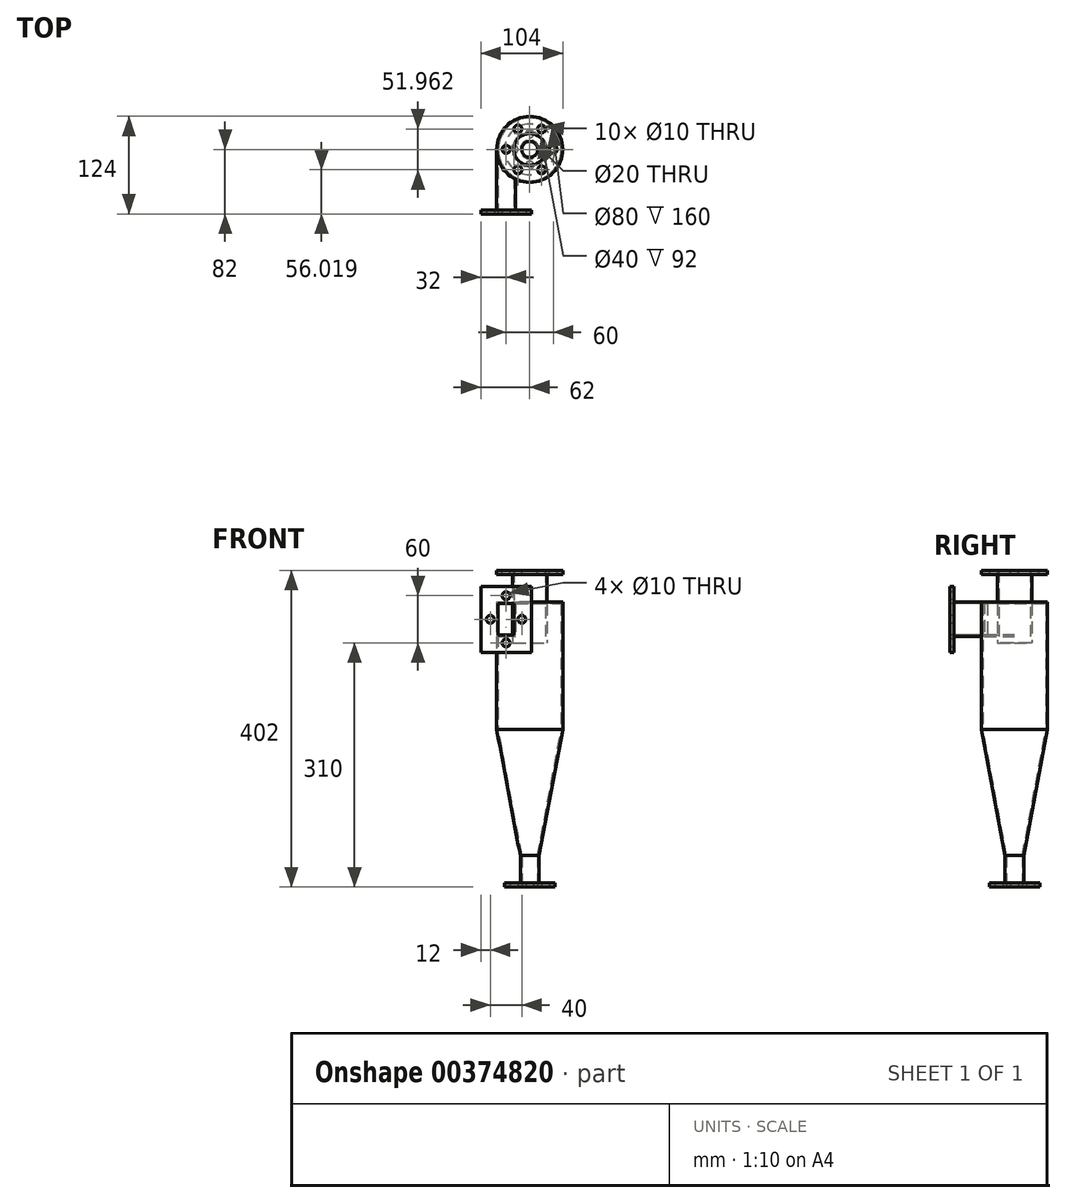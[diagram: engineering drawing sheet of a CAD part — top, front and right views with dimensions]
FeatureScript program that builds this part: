
annotation { "Feature Type Name" : "Feature", "Feature Type Description" : "" }
export const myFeature = defineFeature(function(context is Context, id is Id, definition is map)
    precondition{}
    {
        {
            var Q0;
            Q0=qCreatedBy(makeId("Front.planeOp"),FACE);
            var sketch = newSketch(context, id + "F0", { "sketchPlane" : qUnion([Q0])});
            skLineSegment(sketch, "E0", {"start": v(-40, 360) * mm, "end": v(-40, 200) * mm});
            skLineSegment(sketch, "E1", {"start": v(-40, 200) * mm, "end": v(-10, 40) * mm});
            skLineSegment(sketch, "E2", {"start": v(-10, 40) * mm, "end": v(-10, 0) * mm});
            skLineSegment(sketch, "E3", {"start": v(-40, 360) * mm, "end": v(-22, 360) * mm});
            skLineSegment(sketch, "E4", {"start": v(-10, 0) * mm, "end": v(0, 0) * mm, "construction": true});
            skLineSegment(sketch, "E5", {"start": v(-20, 310) * mm, "end": v(0, 310) * mm, "construction": true});
            skLineSegment(sketch, "E6", {"start": v(0, 0) * mm, "end": v(0, 360) * mm, "construction": true});
            skLineSegment(sketch, "E7.0", {"start": v(-42, 362) * mm, "end": v(-22, 362) * mm});
            skLineSegment(sketch, "E7.1", {"start": v(-42, 362) * mm, "end": v(-42, 199.81) * mm});
            skLineSegment(sketch, "E7.2", {"start": v(-42, 199.81) * mm, "end": v(-12, 39.81) * mm});
            skLineSegment(sketch, "E7.3", {"start": v(-12, 39.81) * mm, "end": v(-12, 0) * mm});
            skLineSegment(sketch, "E8", {"start": v(-22, 362) * mm, "end": v(-22, 402) * mm});
            skLineSegment(sketch, "E9", {"start": v(-22, 402) * mm, "end": v(-20, 402) * mm});
            skLineSegment(sketch, "E10", {"start": v(-20, 402) * mm, "end": v(-20, 360) * mm});
            skLineSegment(sketch, "E11", {"start": v(-20, 310) * mm, "end": v(-20, 310) * mm});
            skLineSegment(sketch, "E12", {"start": v(-12, 0) * mm, "end": v(-10, 0) * mm});
            skLineSegment(sketch, "E13", {"start": v(-22, 360) * mm, "end": v(-22, 310) * mm});
            skLineSegment(sketch, "E14", {"start": v(-20, 310) * mm, "end": v(-22, 310) * mm});
            skPoint(sketch, "E15.end.orphan", {"position": v(-20, 360) * mm});
            skLineSegment(sketch, "E16", {"start": v(-20, 360) * mm, "end": v(-20, 310) * mm});
            skSolve(sketch);
        }
        {
            var Q0;
            Q0=makeQuery(id+"F0.imprint","IMPRINT",FACE,{"disambiguationData":[TD([[makeQuery(id+"F0.imprint","IMPRINT",EDGE,{"derivedFrom":sQuery(id+"F0.wireOp",EDGE,"E0")}),-1.0]])]});
            var Q1;
            Q1=sQuery(id+"F0.wireOp",EDGE,"E6");
            revolve(context, id + "F1", {"entities" : qUnion([Q0]), "axis" : qUnion([Q1]), "revolveType" : RevolveType.FULL});
        }
        {
            var Q0;
            Q0=qCreatedBy(makeId("Front.planeOp"),FACE);
            cPlane(context, id + "F2", {"entities" : qUnion([Q0]), "cplaneType" : CPlaneType.OFFSET, "offset" : 42 * mm, "width" : 152.4 * mm, "height" : 152.4 * mm});
        }
        {
            var Q0;
            Q0=qCreatedBy(id+"F2.planeOp",FACE);
            var sketch = newSketch(context, id + "F3", { "sketchPlane" : qUnion([Q0])});
            skLineSegment(sketch, "E17", {"start": v(0, 0) * mm, "end": v(0, 400.72) * mm, "construction": true});
            skLineSegment(sketch, "E18.bottom", {"start": v(-40, 360) * mm, "end": v(-20, 360) * mm});
            skLineSegment(sketch, "E18.top", {"start": v(-40, 320) * mm, "end": v(-20, 320) * mm});
            skLineSegment(sketch, "E18.left", {"start": v(-40, 360) * mm, "end": v(-40, 320) * mm});
            skLineSegment(sketch, "E18.right", {"start": v(-20, 360) * mm, "end": v(-20, 320) * mm});
            skLineSegment(sketch, "E19.0", {"start": v(-42, 362) * mm, "end": v(-18, 362) * mm});
            skLineSegment(sketch, "E19.1", {"start": v(-42, 362) * mm, "end": v(-42, 318) * mm});
            skLineSegment(sketch, "E19.2", {"start": v(-42, 318) * mm, "end": v(-18, 318) * mm});
            skLineSegment(sketch, "E19.3", {"start": v(-18, 362) * mm, "end": v(-18, 318) * mm});
            skSolve(sketch);
        }
        {
            var Q0;
            Q0=makeQuery(id+"F3.imprint","IMPRINT",FACE,{"disambiguationData":[TD([[makeQuery(id+"F3.imprint","IMPRINT",EDGE,{"derivedFrom":sQuery(id+"F3.wireOp",EDGE,"E18.bottom")}),1.0]])]});
            var Q1;
            Q1=makeQuery(id+"F1.opRevolve","SWEPT_FACE",FACE,{"disambiguationData":[OSD([sQuery(id+"F0.wireOp",EDGE,"E7.1")])]});
            extrude(context, id + "F4", {"entities" : qUnion([Q0]), "operationType" : NewBodyOperationType.ADD, "endBound" : BoundingType.UP_TO_SURFACE, "oppositeDirection" : true, "endBoundEntityFace" : qUnion([Q1]), "depth" : 25.4 * mm});
        }
        {
            var Q0;
            Q0=makeQuery(id+"F4.opExtrude","CAP_FACE",FACE,{"disambiguationData":[OSD([sQuery(id+"F3.wireOp",EDGE,"E18.bottom"),sQuery(id+"F3.wireOp",EDGE,"E18.top"),sQuery(id+"F3.wireOp",EDGE,"E18.left"),sQuery(id+"F3.wireOp",EDGE,"E18.right"),sQuery(id+"F3.wireOp",EDGE,"E19.0"),sQuery(id+"F3.wireOp",EDGE,"E19.1"),sQuery(id+"F3.wireOp",EDGE,"E19.2"),sQuery(id+"F3.wireOp",EDGE,"E19.3")])],"isStart":true});
            var sketch = newSketch(context, id + "F5", { "sketchPlane" : qUnion([Q0])});
            skLineSegment(sketch, "E20", {"start": v(-40, 360) * mm, "end": v(-20, 360) * mm});
            skLineSegment(sketch, "E21", {"start": v(-20, 360) * mm, "end": v(-20, 320) * mm});
            skLineSegment(sketch, "E22", {"start": v(-20, 320) * mm, "end": v(-40, 320) * mm});
            skLineSegment(sketch, "E23", {"start": v(-40, 320) * mm, "end": v(-40, 360) * mm});
            skSolve(sketch);
        }
        {
            var Q0;
            Q0=qSketchRegion(id+"F5",true);
            var Q1;
            Q1=makeQuery(id+"F1.opRevolve","SWEPT_FACE",FACE,{"disambiguationData":[OSD([sQuery(id+"F0.wireOp",EDGE,"E0")])]});
            extrude(context, id + "F6", {"entities" : qUnion([Q0]), "operationType" : NewBodyOperationType.REMOVE, "endBound" : BoundingType.UP_TO_SURFACE, "oppositeDirection" : true, "endBoundEntityFace" : qUnion([Q1]), "depth" : 25.4 * mm});
        }
        {
            var Q0;
            Q0=makeQuery(id+"F4.opExtrude","CAP_FACE",FACE,{"disambiguationData":[OSD([sQuery(id+"F3.wireOp",EDGE,"E18.bottom"),sQuery(id+"F3.wireOp",EDGE,"E18.top"),sQuery(id+"F3.wireOp",EDGE,"E18.left"),sQuery(id+"F3.wireOp",EDGE,"E18.right"),sQuery(id+"F3.wireOp",EDGE,"E19.0"),sQuery(id+"F3.wireOp",EDGE,"E19.1"),sQuery(id+"F3.wireOp",EDGE,"E19.2"),sQuery(id+"F3.wireOp",EDGE,"E19.3")])],"isStart":true});
            extrude(context, id + "F7", {"entities" : qUnion([Q0]), "operationType" : NewBodyOperationType.ADD, "depth" : 40 * mm});
        }
        {
            var Q0;
            Q0=makeQuery(id+"F7.opExtrude","CAP_FACE",FACE,{"disambiguationData":[OSD([sQuery(id+"F3.wireOp",EDGE,"E18.bottom"),sQuery(id+"F3.wireOp",EDGE,"E18.top"),sQuery(id+"F3.wireOp",EDGE,"E18.left"),sQuery(id+"F3.wireOp",EDGE,"E18.right"),sQuery(id+"F3.wireOp",EDGE,"E19.0"),sQuery(id+"F3.wireOp",EDGE,"E19.1"),sQuery(id+"F3.wireOp",EDGE,"E19.2"),sQuery(id+"F3.wireOp",EDGE,"E19.3")])],"isStart":false});
            var sketch = newSketch(context, id + "F8", { "sketchPlane" : qUnion([Q0])});
            skLineSegment(sketch, "E24", {"start": v(-40, 360) * mm, "end": v(-20, 320) * mm, "construction": true});
            skLineSegment(sketch, "E25", {"start": v(-20, 360) * mm, "end": v(-40, 320) * mm, "construction": true});
            skLineSegment(sketch, "E26.bottom", {"start": v(2, 382) * mm, "end": v(-62, 382) * mm});
            skLineSegment(sketch, "E26.top", {"start": v(2, 298) * mm, "end": v(-62, 298) * mm});
            skLineSegment(sketch, "E26.left", {"start": v(2, 382) * mm, "end": v(2, 298) * mm});
            skLineSegment(sketch, "E26.right", {"start": v(-62, 382) * mm, "end": v(-62, 298) * mm});
            skPoint(sketch, "E26.middle", {"position": v(-30, 340) * mm});
            skSolve(sketch);
        }
        {
            var Q0;
            Q0=makeQuery(id+"F8.imprint","IMPRINT",FACE,{"disambiguationData":[TD([[makeQuery(id+"F8.imprint","IMPRINT",EDGE,{"derivedFrom":sQuery(id+"F8.wireOp",EDGE,"E26.bottom")}),1.0]])]});
            extrude(context, id + "F9", {"entities" : qUnion([Q0]), "operationType" : NewBodyOperationType.ADD, "oppositeDirection" : true, "depth" : 5 * mm});
        }
        {
            var Q0;
            Q0=makeQuery(id+"F1.opRevolve","SWEPT_FACE",FACE,{"disambiguationData":[OSD([sQuery(id+"F0.wireOp",EDGE,"E12")])]});
            var sketch = newSketch(context, id + "F10", { "sketchPlane" : qUnion([Q0])});
            skCircle(sketch, "E27", {"center": v(0, 0) * mm, "radius": 32 * mm});
            skSolve(sketch);
        }
        {
            var Q0;
            Q0=makeQuery(id+"F10.imprint","IMPRINT",FACE,{"disambiguationData":[TD([[makeQuery(id+"F10.imprint","IMPRINT",EDGE,{"derivedFrom":sQuery(id+"F10.wireOp",EDGE,"E27")}),1.0]])]});
            extrude(context, id + "F11", {"entities" : qUnion([Q0]), "operationType" : NewBodyOperationType.ADD, "oppositeDirection" : true, "depth" : 5 * mm});
        }
        {
            var Q0;
            {var subQ0=sQuery(id+"F3.wireOp",EDGE,"E19.3");var subQ1=sQuery(id+"F3.wireOp",EDGE,"E19.2");var subQ2=sQuery(id+"F3.wireOp",EDGE,"E19.1");var subQ3=sQuery(id+"F3.wireOp",EDGE,"E19.0");Q0=makeQuery(id+"F9.boolean.opBoolean","MERGE",FACE,{"derivedFrom":[makeQuery(id+"F7.opExtrude","CAP_FACE",FACE,{"disambiguationData":[OSD([sQuery(id+"F3.wireOp",EDGE,"E18.bottom"),sQuery(id+"F3.wireOp",EDGE,"E18.top"),sQuery(id+"F3.wireOp",EDGE,"E18.left"),sQuery(id+"F3.wireOp",EDGE,"E18.right"),subQ3,subQ2,subQ1,subQ0])],"isStart":false}),makeQuery(id+"F9.opExtrude","CAP_FACE",FACE,{"disambiguationData":[OSD([subQ3,subQ2,subQ1,subQ0,sQuery(id+"F8.wireOp",EDGE,"E26.bottom"),sQuery(id+"F8.wireOp",EDGE,"E26.top"),sQuery(id+"F8.wireOp",EDGE,"E26.left"),sQuery(id+"F8.wireOp",EDGE,"E26.right")])],"isStart":true})]});}
            var sketch = newSketch(context, id + "F12", { "sketchPlane" : qUnion([Q0])});
            skLineSegment(sketch, "E28", {"start": v(-40, 360) * mm, "end": v(-20, 320) * mm, "construction": true});
            skLineSegment(sketch, "E29", {"start": v(-20, 360) * mm, "end": v(-40, 320) * mm, "construction": true});
            skLineSegment(sketch, "E30", {"start": v(-30, 340) * mm, "end": v(-30, 370) * mm, "construction": true});
            skPoint(sketch, "E30.endSnap0", {"position": v(-30, 360) * mm});
            skLineSegment(sketch, "E31", {"start": v(-30, 340) * mm, "end": v(-30, 310) * mm, "construction": true});
            skLineSegment(sketch, "E32", {"start": v(-30, 340) * mm, "end": v(-50, 340) * mm, "construction": true});
            skLineSegment(sketch, "E33", {"start": v(-30, 340) * mm, "end": v(-10, 340) * mm, "construction": true});
            skCircle(sketch, "E34", {"center": v(-30, 370) * mm, "radius": 5 * mm});
            skCircle(sketch, "E35", {"center": v(-10, 340) * mm, "radius": 5 * mm});
            skCircle(sketch, "E36", {"center": v(-50, 340) * mm, "radius": 5 * mm});
            skCircle(sketch, "E37", {"center": v(-30, 310) * mm, "radius": 5 * mm});
            skSolve(sketch);
        }
        {
            var Q0;
            Q0=makeQuery(id+"F12.imprint","IMPRINT",FACE,{"disambiguationData":[TD([[makeQuery(id+"F12.imprint","IMPRINT",EDGE,{"derivedFrom":sQuery(id+"F12.wireOp",EDGE,"E34")}),1.0]])]});
            var Q1;
            Q1=makeQuery(id+"F12.imprint","IMPRINT",FACE,{"disambiguationData":[TD([[makeQuery(id+"F12.imprint","IMPRINT",EDGE,{"derivedFrom":sQuery(id+"F12.wireOp",EDGE,"E35")}),1.0]])]});
            var Q2;
            Q2=makeQuery(id+"F12.imprint","IMPRINT",FACE,{"disambiguationData":[TD([[makeQuery(id+"F12.imprint","IMPRINT",EDGE,{"derivedFrom":sQuery(id+"F12.wireOp",EDGE,"E37")}),1.0]])]});
            var Q3;
            Q3=makeQuery(id+"F12.imprint","IMPRINT",FACE,{"disambiguationData":[TD([[makeQuery(id+"F12.imprint","IMPRINT",EDGE,{"derivedFrom":sQuery(id+"F12.wireOp",EDGE,"E36")}),1.0]])]});
            var Q4;
            Q4=makeQuery(id+"F9.opExtrude","CAP_FACE",FACE,{"disambiguationData":[OSD([sQuery(id+"F3.wireOp",EDGE,"E19.0"),sQuery(id+"F3.wireOp",EDGE,"E19.1"),sQuery(id+"F3.wireOp",EDGE,"E19.2"),sQuery(id+"F3.wireOp",EDGE,"E19.3"),sQuery(id+"F8.wireOp",EDGE,"E26.bottom"),sQuery(id+"F8.wireOp",EDGE,"E26.top"),sQuery(id+"F8.wireOp",EDGE,"E26.left"),sQuery(id+"F8.wireOp",EDGE,"E26.right")])],"isStart":false});
            extrude(context, id + "F13", {"entities" : qUnion([Q0, Q1, Q2, Q3]), "operationType" : NewBodyOperationType.REMOVE, "endBound" : BoundingType.UP_TO_SURFACE, "oppositeDirection" : true, "endBoundEntityFace" : qUnion([Q4]), "depth" : 25 * mm});
        }
        {
            var Q0;
            {var subQ0=sQuery(id+"F0.wireOp",EDGE,"E12");Q0=makeQuery(id+"F11.boolean.opBoolean","MERGE",FACE,{"derivedFrom":[makeQuery(id+"F1.opRevolve","SWEPT_FACE",FACE,{"disambiguationData":[OSD([subQ0])]}),makeQuery(id+"F11.opExtrude","CAP_FACE",FACE,{"disambiguationData":[OSD([sQuery(id+"F0.wireOp",EDGE,"E7.3"),subQ0,sQuery(id+"F10.wireOp",EDGE,"E27")])],"isStart":true})]});}
            var sketch = newSketch(context, id + "F14", { "sketchPlane" : qUnion([Q0])});
            skCircle(sketch, "E38", {"center": v(0, 20) * mm, "radius": 5 * mm});
            skCircle(sketch, "E39.1.0", {"center": v(-20, 0) * mm, "radius": 5 * mm});
            skCircle(sketch, "E39.2.0", {"center": v(0, -20) * mm, "radius": 5 * mm});
            skPoint(sketch, "E39.center", {"position": v(0, 0) * mm});
            skCircle(sketch, "E40.1.3.0", {"center": v(20, 0) * mm, "radius": 5 * mm});
            skSolve(sketch);
        }
        {
            var Q0;
            Q0 = qSketchRegion(id + "F14", true);
            var Q1;
            Q1=makeQuery(id+"F11.opExtrude","CAP_FACE",FACE,{"disambiguationData":[OSD([sQuery(id+"F0.wireOp",EDGE,"E7.3"),sQuery(id+"F0.wireOp",EDGE,"E12"),sQuery(id+"F10.wireOp",EDGE,"E27")])],"isStart":false});
            extrude(context, id + "F15", {"entities" : qUnion([Q0]), "operationType" : NewBodyOperationType.REMOVE, "endBound" : BoundingType.UP_TO_SURFACE, "oppositeDirection" : true, "endBoundEntityFace" : qUnion([Q1]), "depth" : 25 * mm});
        }
        {
            var Q0;
            Q0=makeQuery(id+"F1.opRevolve","SWEPT_FACE",FACE,{"disambiguationData":[OSD([sQuery(id+"F0.wireOp",EDGE,"E9")])]});
            var sketch = newSketch(context, id + "F16", { "sketchPlane" : qUnion([Q0])});
            skCircle(sketch, "E41", {"center": v(0, 0) * mm, "radius": 42 * mm});
            skSolve(sketch);
        }
        {
            var Q0;
            Q0=makeQuery(id+"F16.imprint","IMPRINT",FACE,{"disambiguationData":[TD([[makeQuery(id+"F16.imprint","IMPRINT",EDGE,{"derivedFrom":sQuery(id+"F16.wireOp",EDGE,"E41")}),1.0]])]});
            extrude(context, id + "F17", {"entities" : qUnion([Q0]), "operationType" : NewBodyOperationType.ADD, "oppositeDirection" : true, "depth" : 5 * mm});
        }
        {
            var Q0;
            {var subQ0=sQuery(id+"F0.wireOp",EDGE,"E9");Q0=makeQuery(id+"F17.boolean.opBoolean","MERGE",FACE,{"derivedFrom":[makeQuery(id+"F1.opRevolve","SWEPT_FACE",FACE,{"disambiguationData":[OSD([subQ0])]}),makeQuery(id+"F17.opExtrude","CAP_FACE",FACE,{"disambiguationData":[OSD([sQuery(id+"F0.wireOp",EDGE,"E8"),subQ0,sQuery(id+"F16.wireOp",EDGE,"E41")])],"isStart":true})]});}
            var sketch = newSketch(context, id + "F18", { "sketchPlane" : qUnion([Q0])});
            skCircle(sketch, "E42", {"center": v(-30, 0) * mm, "radius": 5 * mm});
            skCircle(sketch, "E43.1.0", {"center": v(-15, -25.98) * mm, "radius": 5 * mm});
            skCircle(sketch, "E43.2.0", {"center": v(15, -25.98) * mm, "radius": 5 * mm});
            skPoint(sketch, "E43.center", {"position": v(0, 0) * mm});
            skCircle(sketch, "E44.1.3.0", {"center": v(30, 0) * mm, "radius": 5 * mm});
            skCircle(sketch, "E44.1.4.0", {"center": v(15, 25.98) * mm, "radius": 5 * mm});
            skCircle(sketch, "E44.1.5.0", {"center": v(-15, 25.98) * mm, "radius": 5 * mm});
            skSolve(sketch);
        }
        {
            var Q0;
            Q0 = qSketchRegion(id + "F18", true);
            var Q1;
            Q1=makeQuery(id+"F17.opExtrude","CAP_FACE",FACE,{"disambiguationData":[OSD([sQuery(id+"F0.wireOp",EDGE,"E8"),sQuery(id+"F0.wireOp",EDGE,"E9"),sQuery(id+"F16.wireOp",EDGE,"E41")])],"isStart":false});
            extrude(context, id + "F19", {"entities" : qUnion([Q0]), "operationType" : NewBodyOperationType.REMOVE, "endBound" : BoundingType.UP_TO_SURFACE, "oppositeDirection" : true, "endBoundEntityFace" : qUnion([Q1]), "depth" : 25 * mm});
        }
    });
